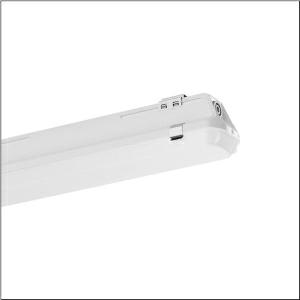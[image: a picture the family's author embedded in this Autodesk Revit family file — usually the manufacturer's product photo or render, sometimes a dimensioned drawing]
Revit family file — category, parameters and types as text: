
# Revit family: monsun_r__11_emergency_51fp10dp468h2_0287
name_source: partatom
category: Lighting Fixtures
units: mm (PartAtom-declared; Revit-internal decimal feet)

## family parameters
Cut with Voids When Loaded = No
Host = Face
Light Source = No
Part Type = Normal
Room Calculation Point = No
Round Connector Dimension = Use Diameter
Shared = No

## types (1)
- --- (1 x LED, 890 lm, 6.9 W, 4000K)
    Apparent Load = 7 VA
    CIE Flux Codes = 47 77 93 94 100
    Color Rendering = 80
    Color Temperature = 4000K
    Default Elevation = 1800 mm
    Description = Monsun® 11 emergency, damp-proof luminaire, chain hanger, primary optical cover: enclosure, of PMMA, light emission: direct distribution, primary light characteristic: symmetric, installation type: suspended mounting, surface-mounted, horizontal mounting, vertical mounting, LED, rated luminous flux: 6.050lm, luminous efficacy: 175lm/W, light colour: 840, colour temperature: 4000K, control gear: ECG DALI, with terminal, 5-pole, max. 2.5mm², mains connection: 220..240V, AC/DC, 0/50..60Hz, rated input power: 35W, luminaire housing, of glass-fibre reinforced polyester, uncoated, bright grey, incl. chain hanger, length: 1.590mm, width: 90mm, height: 88mm, clip for enclosure, of stainless steel (V2A), ceiling mounting element, of stainless steel (V2A), chain hanger, of stainless steel (V2A), protection rating (complete): IP66, insulation class (complete): insulation class I (protective earthing), certification: CE, UKCA, protection symbol: D, impact resistance: IK04, permissible operating ambient temperature: -25..+40°C, standard: EN 60598-2-22, EN 50419, EN 60598-2-1, no direct snow, no direct sun, no direct rain, for indoor or canopied outdoor use, corresponds to IFS (International Featured Standards) requirements for safety and quality in the food industry, contact your sales advisor before using the luminaires in applications with unclear chemical exposure, large temperature fluctuations or condensation-forming humidity, LABS conformity tested according to VDMA 24364:2018-05, packaging unit: 1 piece
    Height = 89 mm
    Lamp = 1 x LED
    Lamp Light Flux = 890 lm
    Lamp Power = 6.9 W
    Lamp count = 1
    Length = 1590 mm
    Luminous efficacy = 129 lm/W
    Manufacturer = Siteco
    ModVariant = No
    Model = 51FP10DP468H2
    Mounting Place = Ceiling
    Mounting Type = Surface mounted
    Number of Poles = 1
    OnlyDefault = Yes
    Power Factor = 1
    Product Name = Monsun® 11 emergency
    Product group = damp-proof luminaire
    ProductGroupID = 300
    Protection Class = Protection class I
    Protection Degree = IP 66
    RLX_Detail_Level = 1
    RLX_Emergency_Light_Flux = 0 lm
    RLX_Emergency_Type = 0
    RLX_Emergency_Type_DB = No
    RlxData = <blob elided: 92785 chars, md5=693a111d>
    Socket = socket
    Standby Power = 0 W
    System Light Flux = 890 lm
    System Power = 7 W
    Type Comments = : equivalent power supply (DC)
    Type Image = l_1004748.jpg
    URL = http://relux.com
    VarID = @adj_134671
    Voltage = 0 V
    Weight = 0.00 kg
    Width = 90 mm

## geometry (parser evidence)
native form markers: Blend x4, Sweep x12
no freeform markers — native parametric forms only
